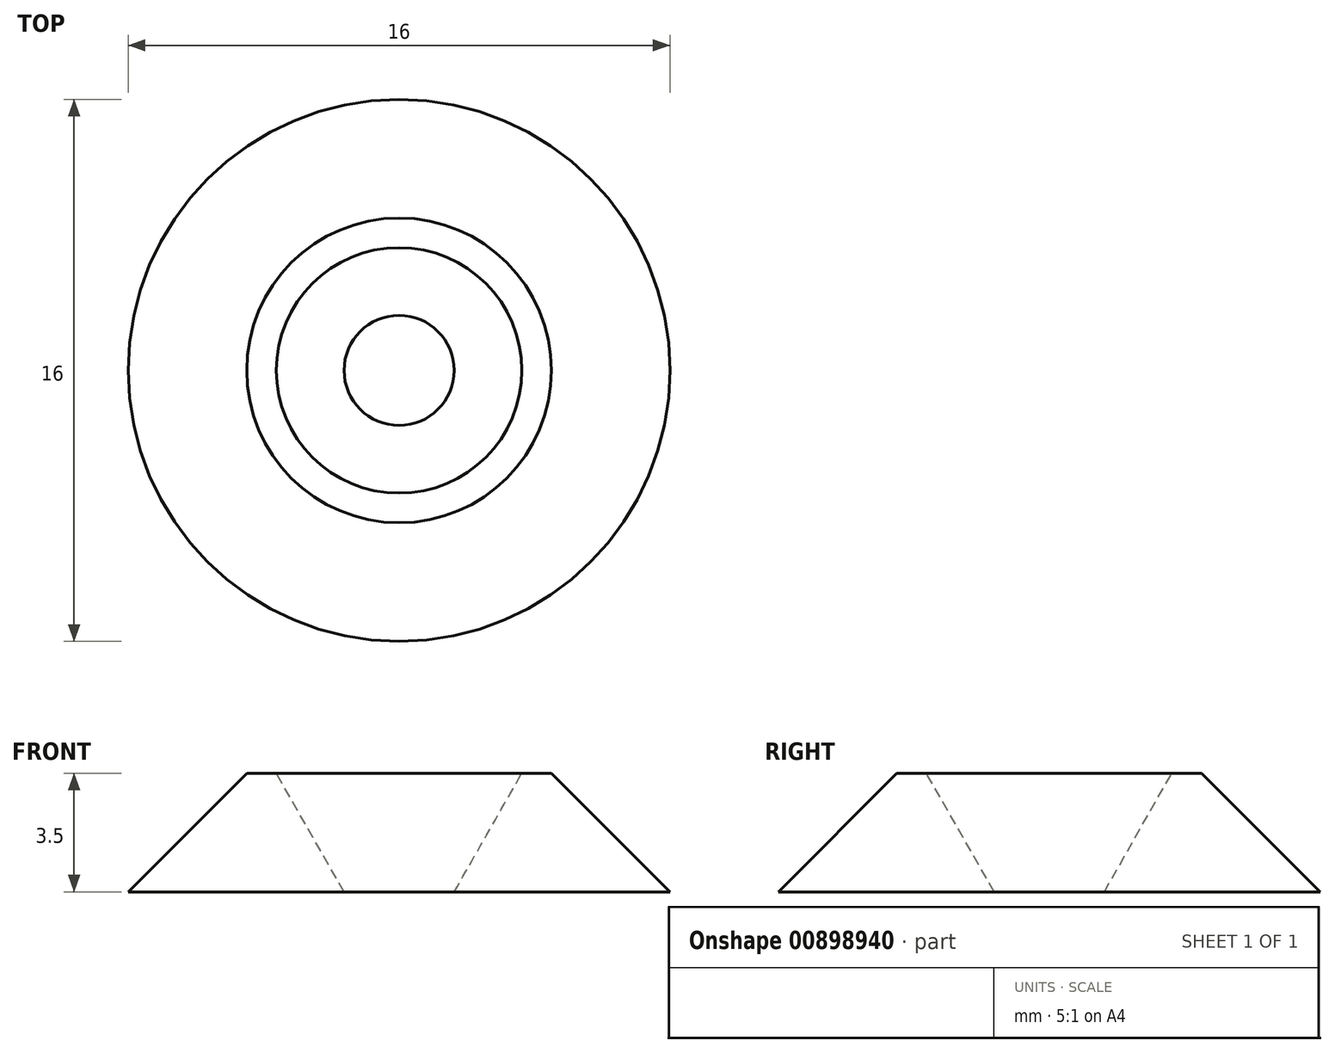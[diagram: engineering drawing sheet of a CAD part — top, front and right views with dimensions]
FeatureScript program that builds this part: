
annotation { "Feature Type Name" : "Feature", "Feature Type Description" : "" }
export const myFeature = defineFeature(function(context is Context, id is Id, definition is map)
    precondition{}
    {
        {
            var Q0;
            Q0=qCreatedBy(makeId("Top.planeOp"),FACE);
            var sketch = newSketch(context, id + "F0", { "sketchPlane" : qUnion([Q0])});
            skCircle(sketch, "E0", {"center": v(0, 0) * mm, "radius": 8 * mm});
            skSolve(sketch);
        }
        {
            var Q0;
            Q0 = qSketchRegion(id + "F0", true);
            extrude(context, id + "F1", {"entities" : qUnion([Q0]), "depth" : 3.5 * mm, "offsetDistance" : 25 * mm});
        }
        {
            var Q0;
            Q0=makeQuery(id+"F1.opExtrude","CAP_EDGE",EDGE,{"disambiguationData":[OSD([sQuery(id+"F0.wireOp",EDGE,"E0")])],"isStart":false});
            chamfer(context, id + "F2", {"entities" : qUnion([Q0]), "width" : 3.5 * mm, "tangentPropagation" : true});
        }
        {
            var Q0;
            Q0=makeQuery(id+"F1.opExtrude","CAP_FACE",FACE,{"disambiguationData":[OSD([sQuery(id+"F0.wireOp",EDGE,"3gmhSflf-BkdG-Dx8z-ejlS-IgLxYmgyftpH"),sQuery(id+"F0.wireOp",EDGE,"E0")])],"isStart":false});
            var sketch = newSketch(context, id + "F3", { "sketchPlane" : qUnion([Q0])});
            skCircle(sketch, "E1", {"center": v(0, 0) * mm, "radius": 3.62 * mm});
            skSolve(sketch);
        }
        {
            var Q0;
            Q0=qCreatedBy(makeId("Top.planeOp"),FACE);
            var sketch = newSketch(context, id + "F4", { "sketchPlane" : qUnion([Q0])});
            skCircle(sketch, "E2", {"center": v(0, 0) * mm, "radius": 1.63 * mm});
            skSolve(sketch);
        }
        {
            var Q1;
            Q1=makeQuery(id+"F3.imprint","IMPRINT",FACE,{"disambiguationData":[TD([[makeQuery(id+"F3.imprint","IMPRINT",EDGE,{"derivedFrom":sQuery(id+"F3.wireOp",EDGE,"E1")}),1.0]])]});
            var Q2;
            Q2=makeQuery(id+"F4.imprint","IMPRINT",FACE,{"disambiguationData":[TD([[makeQuery(id+"F4.imprint","IMPRINT",EDGE,{"derivedFrom":sQuery(id+"F4.wireOp",EDGE,"E2")}),1.0]])]});
            loft(context, id + "F5", {"operationType" : NewBodyOperationType.REMOVE, "sheetProfilesArray" : [{ "sheetProfileEntities" : qUnion([Q1]) }, { "sheetProfileEntities" : qUnion([Q2]) }]});
        }
    });
